# Revit family: EU_SINGLE_IDU_4WAY_CST_L_Ver.1.1
name_source: partatom
category: Mechanical Equipment
revit_build: Autodesk Revit 2016 (Build: 20150220_1215(x64)
units: mm (PartAtom-declared; Revit-internal decimal feet)

## family parameters
Always vertical = Yes
Cut with Voids When Loaded = No
Part Type = Normal
Room Calculation Point = No
Round Connector Dimension = Use Radius
Shared = No
Work Plane-Based = No

## types (17) — shared parameters
Manufacturer = SAMSUNG
URL = www.samsung.com

## per-type parameters (varying)
| type | Model | Net  Weight | Panel Model | Panel Net Weight | Refrigerant Type |
| 9.00 kW,  220-240V, 4WAY CASSETTE | AC090MN4DKH/EU | 18.00 kg | PC4NUSKAN | 5.80 kg | R410A |
| 7.10 kW,  220-240V, 4WAY CASSETTE | AC071JN4CEH/EU | 18.00 kg | PC4NUSKE | 5.90 kg | R410A |
| 10.00 kW,  220-240V, 4WAY CASSETTE | AC100JN4CEH/EU | 20.00 kg | PC4NUSKE | 5.90 kg | R410A |
| 10.0 kW,  220-240V, 4WAY CASSETTE | AC100MN4DKH/EU | 18.00 kg | PC4NUSKAN | 5.80 kg | R410A |
| 12.50 kW,  220-240V, 4WAY CASSETTE | AC125JN4CEH/EU | 20.00 kg | PC4NUSKE | 5.90 kg | R410A |
| 12.00 kW,  220-240V, 4WAY CASSETTE | AC120MN4DKH/EU | 18.00 kg | PC4NUSKAN | 5.80 kg | R410A |
| 13.40 kW,  220-240V, 4WAY CASSETTE | AC140MN4DKH/EU | 20.00 kg | PC4NUSKAN | 5.80 kg | R410A |
| 9.00 kW,  220-240V, 4WAY CASSETTE, WIND FREE | AC090NN4DKH/EU | 18.00 kg | PC4NUSKAN | 6.50 kg | R410A |
| 10.00 kW,  220-240V, 4WAY CASSETTE, WIND FREE | AC100NN4DKH/EU | 18.00 kg | PC4NUFMAN | 6.50 kg | R410A |
| 12.00 kW,  220-240V, 4WAY CASSETTE, WIND FREE | AC120NN4DKH/EU | 18.00 kg | PC4NUFMAN | 6.50 kg | R410A |
| 13.40 kW,  220-240V, 4WAY CASSETTE, WIND FREE | AC140NN4DKH/EU | 18.00 kg | PC4NUFMAN | 6.50 kg | R410A |
| 10.0kW, 220-240V, 4WAY CASSETTE(LRG+), R32, 1phase ODU | AC100RN4DKG/EU | 18.00 kg | PC4NUFMAN | 6.30 kg | R32 |
| 10.0kW, 220-240V, 4WAY CASSETTE(LRG+), R32, 3phase ODU | AC100RN4DKG/EU | 18.00 kg | PC4NUFMAN | 6.30 kg | R32 |
| 12.0kW, 220-240V, 4WAY CASSETTE(LRG+), R32, 1phase ODU | AC120RN4DKG/EU | 18.00 kg | PC4NUFMAN | 6.30 kg | R32 |
| 12.0kW, 220-240V, 4WAY CASSETTE(LRG+), R32, 3phase ODU | AC120RN4DKG/EU | 18.00 kg | PC4NUFMAN | 6.30 kg | R32 |
| 14.0kW, 220-240V, 4WAY CASSETTE(LRG+), R32, 1phase ODU | AC140RN4DKG/EU | 20.00 kg | PC4NUFMAN | 6.30 kg | R32 |
| 14.0kW, 220-240V, 4WAY CASSETTE(LRG+), R32, 3phase ODU | AC140RN4DKG/EU | 20.00 kg | PC4NUFMAN | 6.30 kg | R32 |

## geometry (parser evidence)
native form markers: Sweep x14
no freeform markers — native parametric forms only
